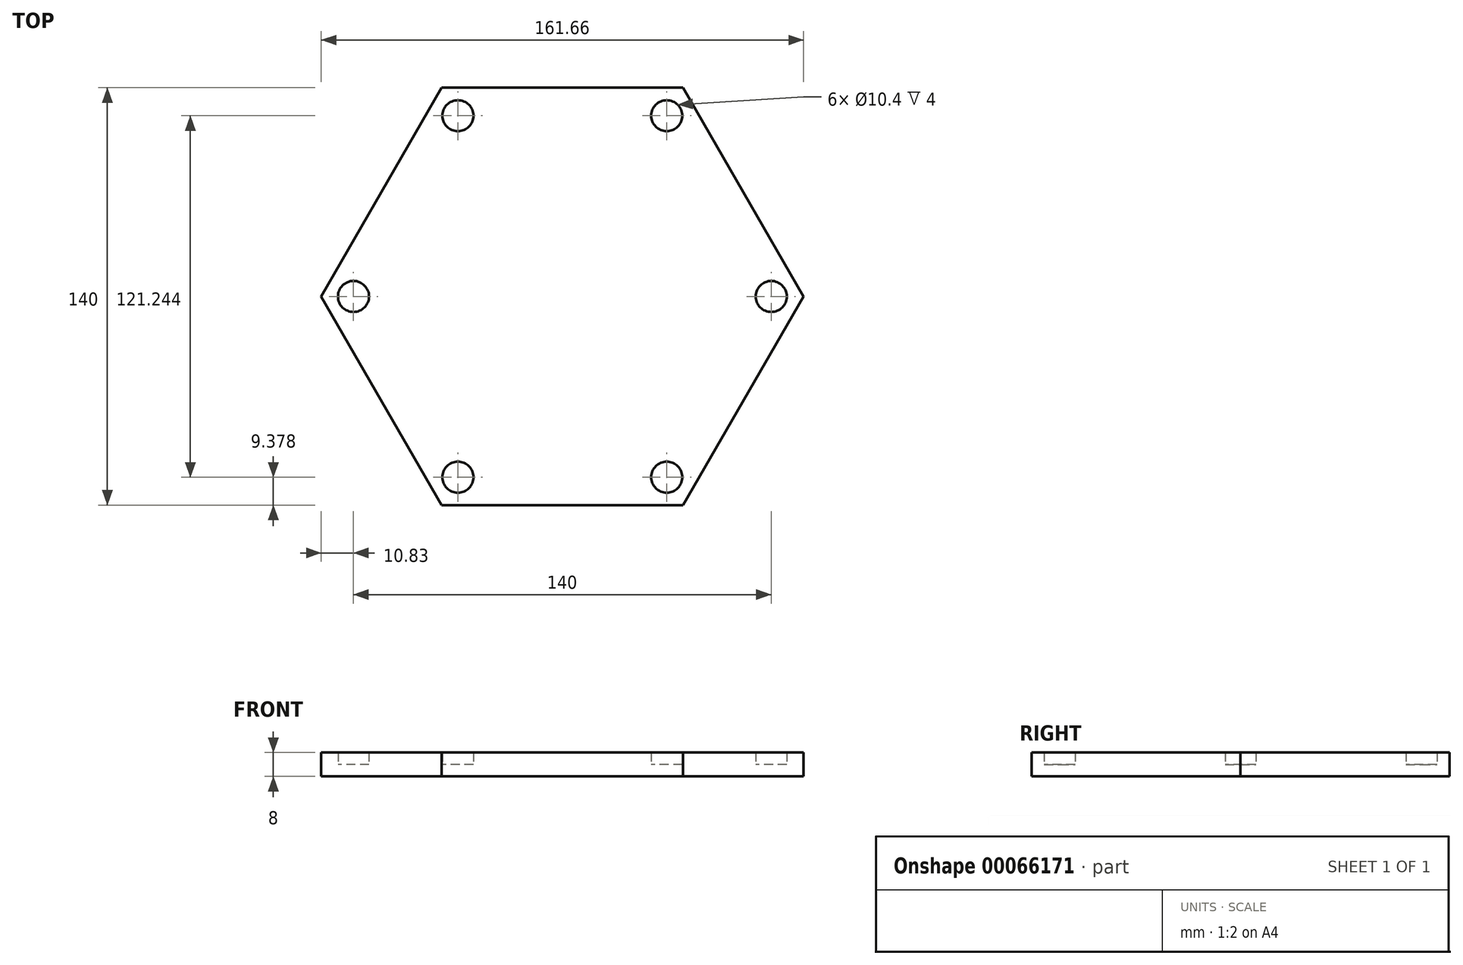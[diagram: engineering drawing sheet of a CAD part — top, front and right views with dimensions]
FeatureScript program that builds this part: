
annotation { "Feature Type Name" : "Feature", "Feature Type Description" : "" }
export const myFeature = defineFeature(function(context is Context, id is Id, definition is map)
    precondition{}
    {
        {
            var Q0;
            Q0=qCreatedBy(makeId("Top.planeOp"),FACE);
            var sketch = newSketch(context, id + "F0", { "sketchPlane" : qUnion([Q0])});
            skCircle(sketch, "E0.cCircle", {"center": v(0, 0) * mm, "radius": 70 * mm, "construction": true});
            skLineSegment(sketch, "E0.0", {"start": v(-40.41, 70) * mm, "end": v(40.41, 70) * mm});
            skLineSegment(sketch, "E0.1", {"start": v(40.41, 70) * mm, "end": v(80.83, 0) * mm});
            skLineSegment(sketch, "E0.2", {"start": v(80.83, 0) * mm, "end": v(40.41, -70) * mm});
            skLineSegment(sketch, "E0.3", {"start": v(40.41, -70) * mm, "end": v(-40.41, -70) * mm});
            skLineSegment(sketch, "E0.4", {"start": v(-40.41, -70) * mm, "end": v(-80.83, 0) * mm});
            skLineSegment(sketch, "E0.5", {"start": v(-80.83, 0) * mm, "end": v(-40.41, 70) * mm});
            skPoint(sketch, "E0.0.midPoint", {"position": v(0, 70) * mm});
            skLineSegment(sketch, "E1", {"start": v(0, 0) * mm, "end": v(-40.41, 70) * mm, "construction": true});
            skCircle(sketch, "E2", {"center": v(-35, 60.62) * mm, "radius": 5.2 * mm});
            skCircle(sketch, "E3.1.0", {"center": v(-70, 0) * mm, "radius": 5.2 * mm});
            skCircle(sketch, "E3.2.0", {"center": v(-35, -60.62) * mm, "radius": 5.2 * mm});
            skCircle(sketch, "E3.3.0", {"center": v(35, -60.62) * mm, "radius": 5.2 * mm});
            skCircle(sketch, "E3.4.0", {"center": v(70, 0) * mm, "radius": 5.2 * mm});
            skCircle(sketch, "E3.5.0", {"center": v(35, 60.62) * mm, "radius": 5.2 * mm});
            skSolve(sketch);
        }
        {
            var Q0;
            Q0=makeQuery(id+"F0.imprint","IMPRINT",FACE,{"disambiguationData":[TD([[makeQuery(id+"F0.imprint","IMPRINT",EDGE,{"derivedFrom":sQuery(id+"F0.wireOp",EDGE,"E3.1.0")}),1.0]])]});
            var Q1;
            Q1=makeQuery(id+"F0.imprint","IMPRINT",FACE,{"disambiguationData":[TD([[makeQuery(id+"F0.imprint","IMPRINT",EDGE,{"derivedFrom":sQuery(id+"F0.wireOp",EDGE,"E2")}),1.0]])]});
            var Q2;
            Q2=makeQuery(id+"F0.imprint","IMPRINT",FACE,{"disambiguationData":[TD([[makeQuery(id+"F0.imprint","IMPRINT",EDGE,{"derivedFrom":sQuery(id+"F0.wireOp",EDGE,"E3.5.0")}),1.0]])]});
            var Q3;
            Q3=makeQuery(id+"F0.imprint","IMPRINT",FACE,{"disambiguationData":[TD([[makeQuery(id+"F0.imprint","IMPRINT",EDGE,{"derivedFrom":sQuery(id+"F0.wireOp",EDGE,"E3.4.0")}),1.0]])]});
            var Q4;
            Q4=makeQuery(id+"F0.imprint","IMPRINT",FACE,{"disambiguationData":[TD([[makeQuery(id+"F0.imprint","IMPRINT",EDGE,{"derivedFrom":sQuery(id+"F0.wireOp",EDGE,"E3.3.0")}),1.0]])]});
            var Q5;
            Q5=makeQuery(id+"F0.imprint","IMPRINT",FACE,{"disambiguationData":[TD([[makeQuery(id+"F0.imprint","IMPRINT",EDGE,{"derivedFrom":sQuery(id+"F0.wireOp",EDGE,"E3.2.0")}),1.0]])]});
            var Q6;
            Q6=makeQuery(id+"F0.imprint","IMPRINT",FACE,{"disambiguationData":[TD([[makeQuery(id+"F0.imprint","IMPRINT",EDGE,{"derivedFrom":sQuery(id+"F0.wireOp",EDGE,"E0.0")}),-1.0]])]});
            var Q7;
            Q7=makeQuery(id+"F0.imprint","IMPRINT",FACE,{"disambiguationData":[TD([[makeQuery(id+"F0.imprint","IMPRINT",EDGE,{"derivedFrom":sQuery(id+"F0.wireOp",EDGE,"E0.0")}),-1.0]])]});
            extrude(context, id + "F1", {"entities" : qUnion([Q0, Q1, Q2, Q3, Q4, Q5, Q6, Q7]), "oppositeDirection" : true, "depth" : 4 * mm});
        }
        {
            var Q0;
            Q0 = qSketchRegion(id + "F0", true);
            extrude(context, id + "F2", {"entities" : qUnion([Q0]), "operationType" : NewBodyOperationType.ADD, "depth" : 4 * mm});
        }
    });
